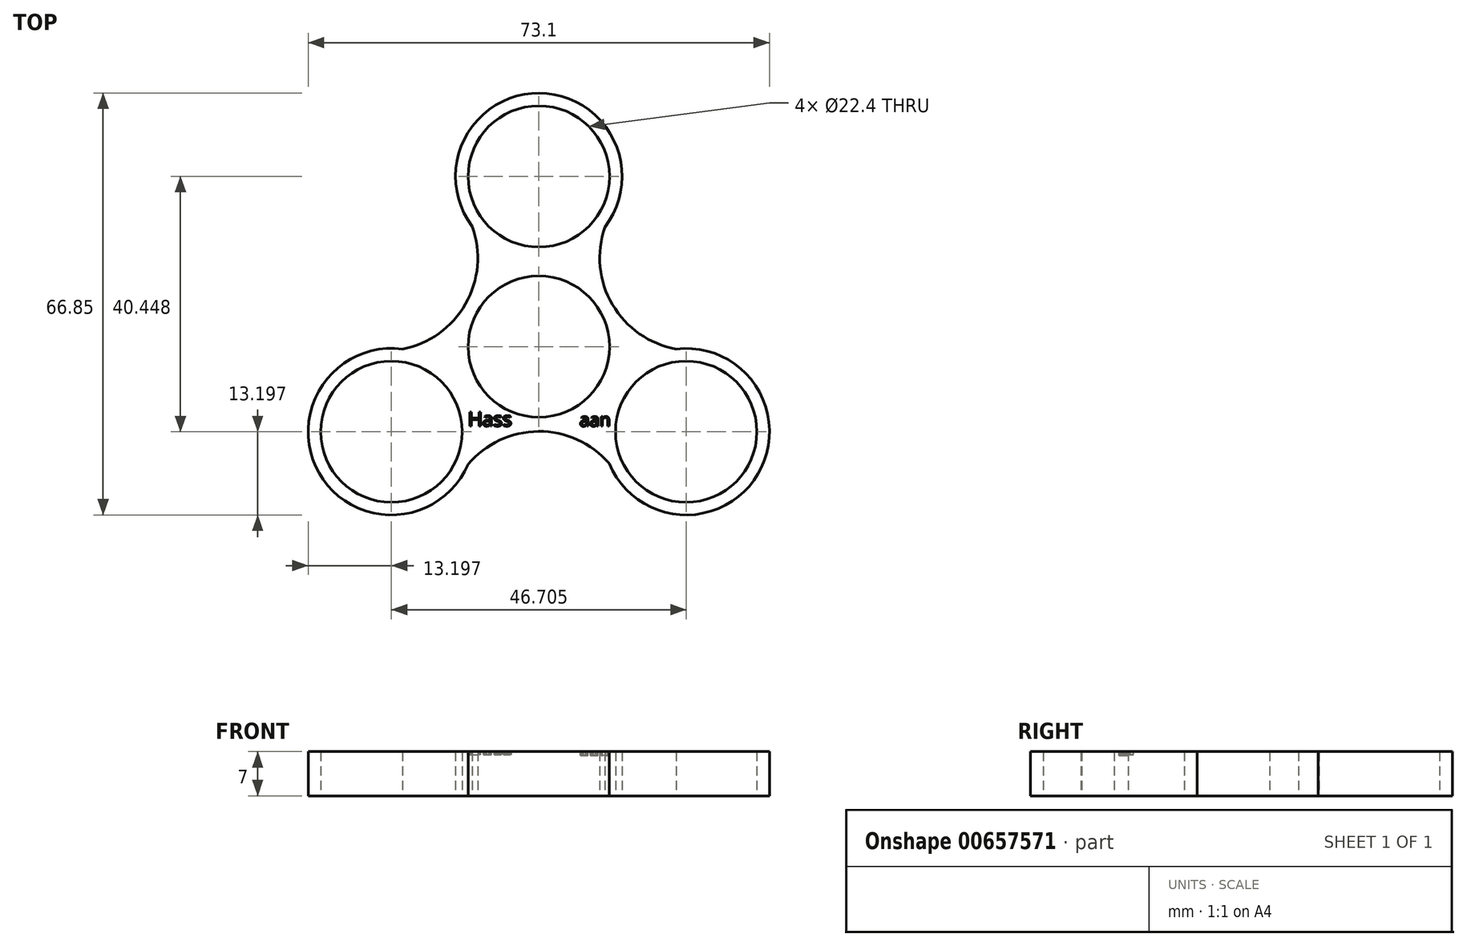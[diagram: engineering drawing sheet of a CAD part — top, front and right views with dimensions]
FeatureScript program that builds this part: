
annotation { "Feature Type Name" : "Feature", "Feature Type Description" : "" }
export const myFeature = defineFeature(function(context is Context, id is Id, definition is map)
    precondition{}
    {
        {
            var Q0;
            Q0=qCreatedBy(makeId("Top.planeOp"),FACE);
            var sketch = newSketch(context, id + "F0", { "sketchPlane" : qUnion([Q0])});
            skCircle(sketch, "E0", {"center": v(0, 0) * mm, "radius": 11.2 * mm});
            skArc(sketch, "E1", {"start": v(10.47, 18.92) * mm, "mid": v(0.07, 40.17) * mm, "end": v(-10.55, 19.03) * mm});
            skCircle(sketch, "E2", {"center": v(0, 26.97) * mm, "radius": 11.2 * mm});
            skArc(sketch, "E3.1.0", {"start": v(-21.62, -0.4) * mm, "mid": v(-34.82, -20.02) * mm, "end": v(-11.2, -18.66) * mm});
            skCircle(sketch, "E3.1.1", {"center": v(-23.35, -13.48) * mm, "radius": 11.2 * mm});
            skArc(sketch, "E3.2.0", {"start": v(11.15, -18.52) * mm, "mid": v(34.75, -20.14) * mm, "end": v(21.76, -0.38) * mm});
            skCircle(sketch, "E3.2.1", {"center": v(23.35, -13.48) * mm, "radius": 11.2 * mm});
            skArc(sketch, "E4", {"start": v(10.47, 18.92) * mm, "mid": v(11.66, 6.67) * mm, "end": v(21.76, -0.38) * mm});
            skArc(sketch, "E5.1.0", {"start": v(-21.62, -0.4) * mm, "mid": v(-11.6, 6.77) * mm, "end": v(-10.55, 19.03) * mm});
            skArc(sketch, "E5.2.0", {"start": v(11.15, -18.52) * mm, "mid": v(-0.06, -13.43) * mm, "end": v(-11.2, -18.66) * mm});
            skPoint(sketch, "E6.endSnap0", {"position": v(0.07, 40.17) * mm});
            skSolve(sketch);
        }
        {
            var Q0;
            Q0=makeQuery(id+"F0.imprint","IMPRINT",FACE,{"disambiguationData":[TD([[makeQuery(id+"F0.imprint","IMPRINT",EDGE,{"derivedFrom":sQuery(id+"F0.wireOp",EDGE,"E0")}),-1.0]])]});
            extrude(context, id + "F1", {"entities" : qUnion([Q0]), "depth" : 7 * mm, "offsetDistance" : 25 * mm});
        }
        {
            var Q0;
            Q0=makeQuery(id+"F1.opExtrude","CAP_FACE",FACE,{"disambiguationData":[OSD([sQuery(id+"F0.wireOp",EDGE,"E0"),sQuery(id+"F0.wireOp",EDGE,"E1"),sQuery(id+"F0.wireOp",EDGE,"E2"),sQuery(id+"F0.wireOp",EDGE,"E3.1.0"),sQuery(id+"F0.wireOp",EDGE,"E3.1.1"),sQuery(id+"F0.wireOp",EDGE,"E3.2.0"),sQuery(id+"F0.wireOp",EDGE,"E3.2.1"),sQuery(id+"F0.wireOp",EDGE,"E4"),sQuery(id+"F0.wireOp",EDGE,"E5.1.0"),sQuery(id+"F0.wireOp",EDGE,"E5.2.0")])],"isStart":false});
            var sketch = newSketch(context, id + "F2", { "sketchPlane" : qUnion([Q0])});
            skText(sketch, "E7", { "text": "Hass", "fontName": "OpenSans-Regular.ttf"});
            const initialGuessF2  = {"E7": [-0.01121, -0.0126, 1, 0, 0.00222]};
            skSetInitialGuess(sketch, initialGuessF2);
            skSolve(sketch);
        }
        {
            var Q0;
            Q0 = qSketchRegion(id + "F2", true);
            extrude(context, id + "F3", {"entities" : qUnion([Q0]), "operationType" : NewBodyOperationType.REMOVE, "oppositeDirection" : true, "depth" : 0.51 * mm, "offsetDistance" : 25 * mm});
        }
        {
            var Q0;
            {var subQ0=sQuery(id+"F0.wireOp",EDGE,"E5.1.0");var subQ1=sQuery(id+"F0.wireOp",EDGE,"E4");var subQ2=sQuery(id+"F0.wireOp",EDGE,"E3.2.1");var subQ3=sQuery(id+"F0.wireOp",EDGE,"E3.2.0");var subQ4=sQuery(id+"F0.wireOp",EDGE,"E3.1.1");var subQ5=sQuery(id+"F0.wireOp",EDGE,"E5.2.0");var subQ6=sQuery(id+"F0.wireOp",EDGE,"E0");var subQ7=sQuery(id+"F0.wireOp",EDGE,"E3.1.0");var subQ8=sQuery(id+"F0.wireOp",EDGE,"E1");var subQ9=sQuery(id+"F0.wireOp",EDGE,"E2");Q0=makeQuery(id+"F3.boolean.opBoolean","SPLIT",FACE,{"disambiguationData":[TD([makeQuery(id+"F1.opExtrude","SWEPT_FACE",FACE,{"disambiguationData":[OSD([subQ6])]})])],"derivedFrom":makeQuery(id+"F1.opExtrude","CAP_FACE",FACE,{"disambiguationData":[OSD([subQ6,subQ8,subQ9,subQ7,subQ4,subQ3,subQ2,subQ1,subQ0,subQ5])],"isStart":false})});}
            var sketch = newSketch(context, id + "F4", { "sketchPlane" : qUnion([Q0])});
            skText(sketch, "E8", { "text": "aan", "fontName": "OpenSans-Regular.ttf"});
            const initialGuessF4  = {"E8": [0.00646, -0.01262, 1, 0, 0.00205]};
            skSetInitialGuess(sketch, initialGuessF4);
            skSolve(sketch);
        }
        {
            var Q0;
            Q0 = qSketchRegion(id + "F4", true);
            extrude(context, id + "F5", {"entities" : qUnion([Q0]), "operationType" : NewBodyOperationType.REMOVE, "oppositeDirection" : true, "depth" : 0.64 * mm, "offsetDistance" : 25 * mm});
        }
    });
